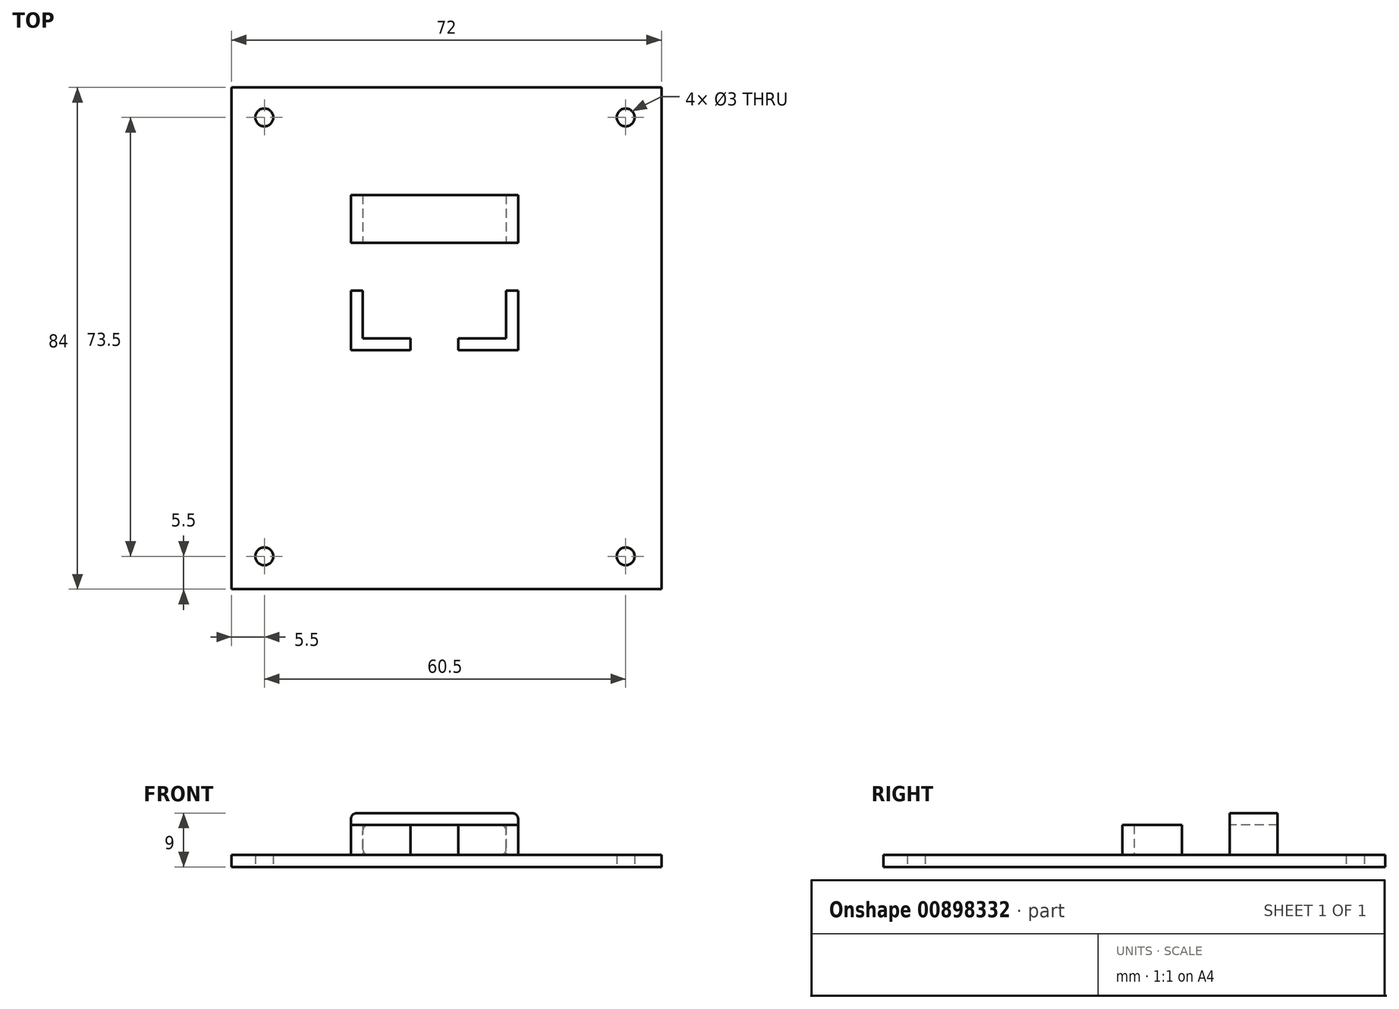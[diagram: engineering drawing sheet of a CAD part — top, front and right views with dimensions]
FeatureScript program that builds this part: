
annotation { "Feature Type Name" : "Feature", "Feature Type Description" : "" }
export const myFeature = defineFeature(function(context is Context, id is Id, definition is map)
    precondition{}
    {
        {
            var Q0;
            Q0=qCreatedBy(makeId("Top.planeOp"),FACE);
            var sketch = newSketch(context, id + "F0", { "sketchPlane" : qUnion([Q0])});
            skPoint(sketch, "E0.middle", {"position": v(0, 0) * mm});
            skLineSegment(sketch, "E1.bottom", {"start": v(-36, 42) * mm, "end": v(36, 42) * mm});
            skLineSegment(sketch, "E1.top", {"start": v(-36, -42) * mm, "end": v(36, -42) * mm});
            skLineSegment(sketch, "E1.left", {"start": v(-36, 42) * mm, "end": v(-36, -42) * mm});
            skLineSegment(sketch, "E1.right", {"start": v(36, 42) * mm, "end": v(36, -42) * mm});
            skCircle(sketch, "E2", {"center": v(-30.5, 37) * mm, "radius": 1.5 * mm});
            skCircle(sketch, "E3", {"center": v(30, 37) * mm, "radius": 1.5 * mm});
            skCircle(sketch, "E4", {"center": v(30, -36.5) * mm, "radius": 1.5 * mm});
            skCircle(sketch, "E5", {"center": v(-30.5, -36.5) * mm, "radius": 1.5 * mm});
            skSolve(sketch);
        }
        {
            var Q0;
            Q0=makeQuery(id+"F0.imprint","IMPRINT",FACE,{"disambiguationData":[TD([[makeQuery(id+"F0.imprint","IMPRINT",EDGE,{"derivedFrom":sQuery(id+"F0.wireOp",EDGE,"E1.bottom")}),-1.0]])]});
            extrude(context, id + "F1", {"entities" : qUnion([Q0]), "depth" : 2 * mm, "offsetDistance" : 25 * mm});
        }
        {
            var Q0;
            Q0=makeQuery(id+"F1.opExtrude","CAP_FACE",FACE,{"disambiguationData":[OSD([sQuery(id+"F0.wireOp",EDGE,"E1.bottom"),sQuery(id+"F0.wireOp",EDGE,"E1.top"),sQuery(id+"F0.wireOp",EDGE,"E1.left"),sQuery(id+"F0.wireOp",EDGE,"E1.right"),sQuery(id+"F0.wireOp",EDGE,"E2"),sQuery(id+"F0.wireOp",EDGE,"E3"),sQuery(id+"F0.wireOp",EDGE,"E4"),sQuery(id+"F0.wireOp",EDGE,"E5")])],"isStart":false});
            var sketch = newSketch(context, id + "F2", { "sketchPlane" : qUnion([Q0])});
            skLineSegment(sketch, "E6.bottom", {"start": v(-16, 24) * mm, "end": v(12, 24) * mm});
            skLineSegment(sketch, "E6.top", {"start": v(-16, 16) * mm, "end": v(12, 16) * mm});
            skLineSegment(sketch, "E6.left", {"start": v(-16, 24) * mm, "end": v(-16, 16) * mm});
            skLineSegment(sketch, "E6.right", {"start": v(12, 24) * mm, "end": v(12, 16) * mm});
            skLineSegment(sketch, "E7.bottom", {"start": v(-14, 35) * mm, "end": v(10, 35) * mm});
            skLineSegment(sketch, "E7.top", {"start": v(-14, 0) * mm, "end": v(10, 0) * mm});
            skLineSegment(sketch, "E7.left", {"start": v(-14, 35) * mm, "end": v(-14, 0) * mm});
            skLineSegment(sketch, "E7.right", {"start": v(10, 35) * mm, "end": v(10, 0) * mm});
            skLineSegment(sketch, "E8", {"start": v(-14, 8) * mm, "end": v(-16, 8) * mm});
            skLineSegment(sketch, "E9", {"start": v(-16, 8) * mm, "end": v(-16, -2) * mm});
            skLineSegment(sketch, "E10", {"start": v(-16, -2) * mm, "end": v(-6, -2) * mm});
            skLineSegment(sketch, "E11", {"start": v(-6, -2) * mm, "end": v(-6, 0) * mm});
            skLineSegment(sketch, "E12.MirrorCS", {"start": v(12, -2) * mm, "end": v(2, -2) * mm});
            skLineSegment(sketch, "E13.MirrorCS", {"start": v(2, -2) * mm, "end": v(2, 0) * mm});
            skLineSegment(sketch, "E14.MirrorCS", {"start": v(12, 8) * mm, "end": v(12, -2) * mm});
            skLineSegment(sketch, "E15.MirrorCS", {"start": v(10, 8) * mm, "end": v(12, 8) * mm});
            skSolve(sketch);
        }
        {
            var Q0;
            Q0=makeQuery(id+"F2.imprint","IMPRINT",FACE,{"disambiguationData":[TD([[makeQuery(id+"F2.imprint","IMPRINT",EDGE,{"derivedFrom":sQuery(id+"F2.wireOp",EDGE,"E6.bottom")}),-1.0]])]});
            extrude(context, id + "F3", {"entities" : qUnion([Q0]), "operationType" : NewBodyOperationType.ADD, "depth" : 7 * mm, "offsetDistance" : 25 * mm});
        }
        {
            var Q0;
            Q0=makeQuery(id+"F3.opExtrude","SWEPT_FACE",FACE,{"disambiguationData":[OSD([sQuery(id+"F2.wireOp",EDGE,"E6.top")])]});
            var sketch = newSketch(context, id + "F4", { "sketchPlane" : qUnion([Q0])});
            skPoint(sketch, "E16.oppositeSnap0", {"position": v(-16, 5.5) * mm});
            skLineSegment(sketch, "E17.bottom", {"start": v(-14, 2) * mm, "end": v(10, 2) * mm});
            skLineSegment(sketch, "E17.top", {"start": v(-14, 7) * mm, "end": v(10, 7) * mm});
            skLineSegment(sketch, "E17.left", {"start": v(-14, 2) * mm, "end": v(-14, 7) * mm});
            skLineSegment(sketch, "E17.right", {"start": v(10, 2) * mm, "end": v(10, 7) * mm});
            skSolve(sketch);
        }
        {
            var Q0;
            Q0=makeQuery(id+"F4.imprint","IMPRINT",FACE,{"disambiguationData":[TD([[makeQuery(id+"F4.imprint","IMPRINT",EDGE,{"derivedFrom":sQuery(id+"F4.wireOp",EDGE,"E17.bottom")}),1.0]])]});
            extrude(context, id + "F5", {"entities" : qUnion([Q0]), "operationType" : NewBodyOperationType.REMOVE, "endBound" : BoundingType.UP_TO_NEXT, "oppositeDirection" : true, "depth" : 25 * mm, "offsetDistance" : 25 * mm});
        }
        {
            var Q0;
            Q0=makeQuery(id+"F5.boolean.opBoolean","COPY",EDGE,{"derivedFrom":makeQuery(id+"F5.opExtrude","SWEPT_EDGE",EDGE,{"disambiguationData":[OSD([sQuery(id+"F4.wireOp",EDGE,"E17.top"),sQuery(id+"F4.wireOp",EDGE,"E17.left")])]})});
            var Q1;
            Q1=makeQuery(id+"F5.boolean.opBoolean","COPY",EDGE,{"derivedFrom":makeQuery(id+"F5.opExtrude","SWEPT_EDGE",EDGE,{"disambiguationData":[OSD([sQuery(id+"F4.wireOp",EDGE,"E17.top"),sQuery(id+"F4.wireOp",EDGE,"E17.right")])]})});
            var Q2;
            Q2=makeQuery(id+"F3.opExtrude","CAP_EDGE",EDGE,{"disambiguationData":[OSD([sQuery(id+"F2.wireOp",EDGE,"E6.right")])],"isStart":false});
            var Q3;
            Q3=makeQuery(id+"F3.opExtrude","CAP_EDGE",EDGE,{"disambiguationData":[OSD([sQuery(id+"F2.wireOp",EDGE,"E6.left")])],"isStart":false});
            var Q4;
            Q4=makeQuery(id+"F3.opExtrude","CAP_EDGE",EDGE,{"disambiguationData":[OSD([sQuery(id+"F2.wireOp",EDGE,"E6.left")])],"isStart":true});
            var Q5;
            Q5=makeQuery(id+"F5.boolean.opBoolean","COPY",EDGE,{"derivedFrom":makeQuery(id+"F5.opExtrude","SWEPT_EDGE",EDGE,{"disambiguationData":[OSD([sQuery(id+"F2.wireOp",EDGE,"E6.top"),sQuery(id+"F4.wireOp",EDGE,"E17.bottom"),sQuery(id+"F4.wireOp",EDGE,"E17.left")])]})});
            var Q6;
            Q6=makeQuery(id+"F5.boolean.opBoolean","COPY",EDGE,{"derivedFrom":makeQuery(id+"F5.opExtrude","SWEPT_EDGE",EDGE,{"disambiguationData":[OSD([sQuery(id+"F2.wireOp",EDGE,"E6.top"),sQuery(id+"F4.wireOp",EDGE,"E17.bottom"),sQuery(id+"F4.wireOp",EDGE,"E17.right")])]})});
            var Q7;
            Q7=makeQuery(id+"F3.opExtrude","CAP_EDGE",EDGE,{"disambiguationData":[OSD([sQuery(id+"F2.wireOp",EDGE,"E6.right")])],"isStart":true});
            fillet(context, id + "F6", {"entities" : qUnion([Q0, Q1, Q2, Q3, Q4, Q5, Q6, Q7]), "radius" : 1 * mm, "tangentPropagation" : true, "allowEdgeOverflow" : false});
        }
        {
            var Q0;
            Q0=makeQuery(id+"F2.imprint","IMPRINT",FACE,{"disambiguationData":[TD([[makeQuery(id+"F2.imprint","IMPRINT",EDGE,{"derivedFrom":sQuery(id+"F2.wireOp",EDGE,"E12.MirrorCS")}),-1.0]])]});
            var Q1;
            {var subQ0=sQuery(id+"F2.wireOp",EDGE,"E8");Q1=makeQuery(id+"F2.imprint","IMPRINT",FACE,{"disambiguationData":[TD([[makeQuery(id+"F2.imprint","IMPRINT",EDGE,{"derivedFrom":subQ0}),1.0]])]});}
            extrude(context, id + "F7", {"entities" : qUnion([Q0, Q1]), "operationType" : NewBodyOperationType.ADD, "depth" : 5 * mm, "offsetDistance" : 25 * mm});
        }
    });
